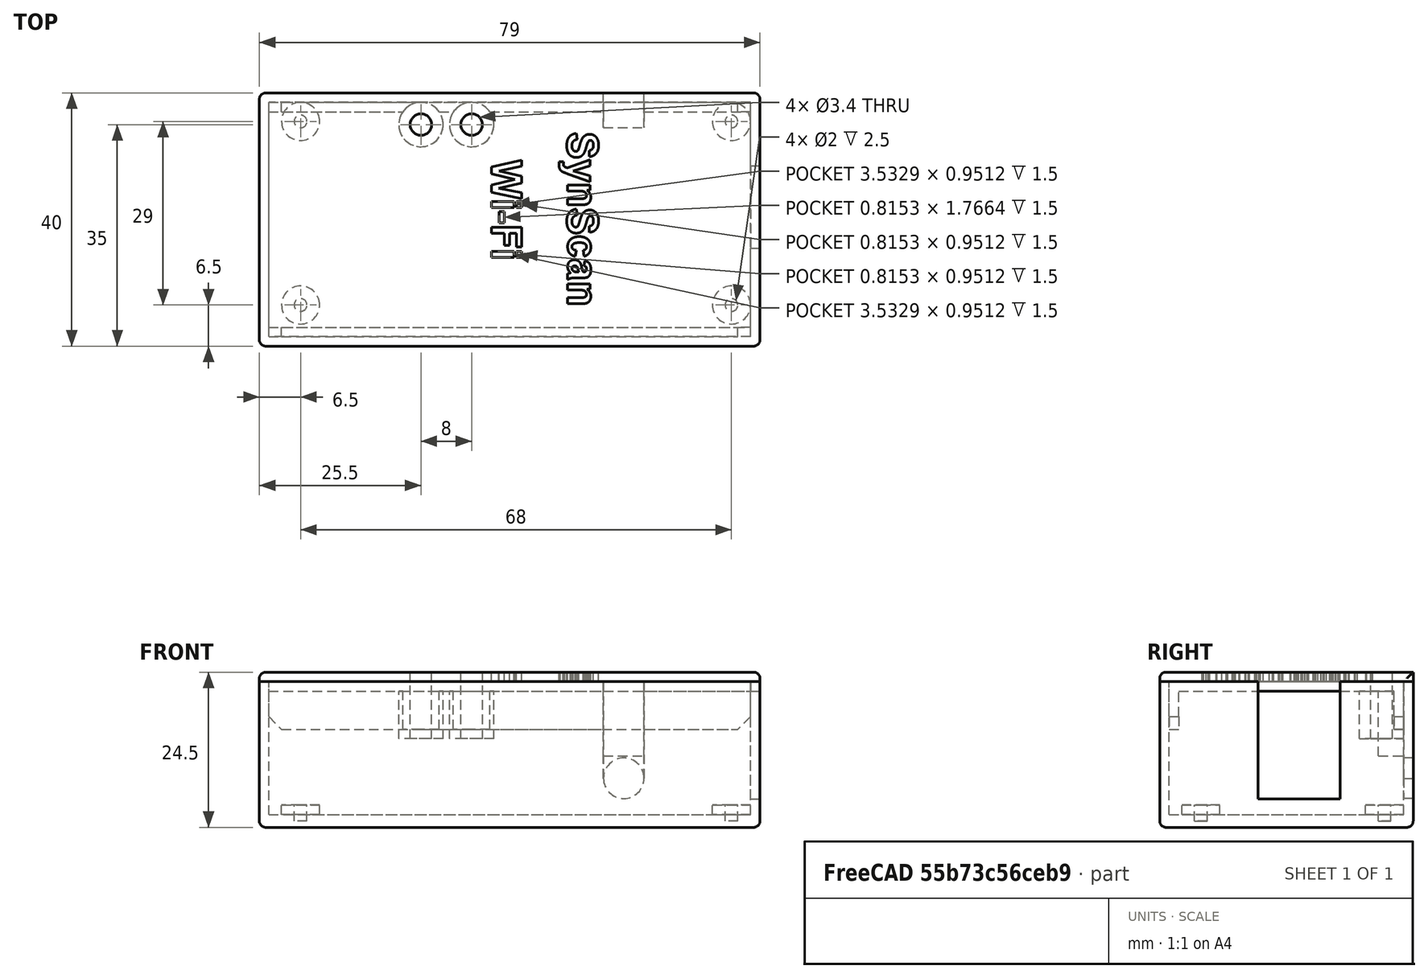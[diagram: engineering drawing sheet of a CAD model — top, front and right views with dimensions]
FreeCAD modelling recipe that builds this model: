
FCSTD DOCUMENT  (FreeCAD 0.17R13387 (Git))
Label: SynScanWiFi
License: All rights reserved
LicenseURL: http://en.wikipedia.org/wiki/All_rights_reserved
objects: Part::Cylinder×16, Part::Box×10, Part::MultiFuse×10, Part::Cut×6, Part::Part2DObjectPython×2, Part::Extrusion×2, Part::Fillet×2, Part::Chamfer×1
note: 49 computed .brp shape members not serialized (recipe doc carries the construction recipe); baked Part::Feature solids carry a one-line shape summary decoded from their .brp

FEATURE [Part::Box] Box  label="Krychle"
  AttacherType = Attacher::AttachEngine3D
  Height = 21
  Length = 76
  Placement = pos=(-39,-19.5,1.5) rot=(0,0,1;0rad)
  Width = 37
FEATURE [Part::Box] Box001  label="Krychle001"
  AttacherType = Attacher::AttachEngine3D
  Height = 23
  Length = 79
  Placement = pos=(-40.5,-21,-0.5) rot=(0,0,1;0rad)
  Width = 40
FEATURE [Part::Cut] Cut
  Base = -> Box001
  Tool = -> Box
FEATURE [Part::Cylinder] Cylinder  label="Válec"
  Angle = 360
  AttacherType = Attacher::AttachEngine3D
  Height = 3
  Placement = pos=(34,14.5,0) rot=(0,0,1;0rad)
  Radius = 1
FEATURE [Part::Cylinder] Cylinder001  label="Válec001"
  Angle = 360
  AttacherType = Attacher::AttachEngine3D
  Height = 3
  Placement = pos=(34,-14.5,0) rot=(0,0,1;0rad)
  Radius = 1
FEATURE [Part::Cylinder] Cylinder002  label="Válec002"
  Angle = 360
  AttacherType = Attacher::AttachEngine3D
  Height = 3
  Placement = pos=(-34,-14.5,0) rot=(0,0,1;0rad)
  Radius = 1
FEATURE [Part::Cylinder] Cylinder003  label="Válec003"
  Angle = 360
  AttacherType = Attacher::AttachEngine3D
  Height = 3
  Placement = pos=(-34,14.5,0) rot=(0,0,1;0rad)
  Radius = 1
FEATURE [Part::MultiFuse] Fusion  label="Diry"
  Placement = pos=(0,0,0.5) rot=(0,0,1;0rad)
  Shapes = -> [Cylinder002,Cylinder,Cylinder003,Cylinder001]
FEATURE [Part::Cylinder] Cylinder004  label="Válec004"
  Angle = 360
  AttacherType = Attacher::AttachEngine3D
  Height = 3
  Placement = pos=(34,14.5,0) rot=(0,0,1;0rad)
  Radius = 3
FEATURE [Part::Cylinder] Cylinder005  label="Válec005"
  Angle = 360
  AttacherType = Attacher::AttachEngine3D
  Height = 3
  Placement = pos=(34,-14.5,0) rot=(0,0,1;0rad)
  Radius = 3
FEATURE [Part::Cylinder] Cylinder006  label="Válec006"
  Angle = 360
  AttacherType = Attacher::AttachEngine3D
  Height = 3
  Placement = pos=(-34,14.5,0) rot=(0,0,1;0rad)
  Radius = 3
FEATURE [Part::Cylinder] Cylinder007  label="Válec007"
  Angle = 360
  AttacherType = Attacher::AttachEngine3D
  Height = 3
  Placement = pos=(-34,-14.5,0) rot=(0,0,1;0rad)
  Radius = 3
FEATURE [Part::MultiFuse] Fusion001
  Shapes = -> [Cylinder007,Cylinder004,Cylinder006,Cylinder005]
FEATURE [Part::Box] Box002  label="Krychle002"
  AttacherType = Attacher::AttachEngine3D
  Height = 19
  Length = 10
  Placement = pos=(30,-5.5,4) rot=(0,0,1;0rad)
  Width = 13
FEATURE [Part::Cylinder] Cylinder008  label="j1"
  Angle = 360
  AttacherType = Attacher::AttachEngine3D
  Height = 10
  Placement = pos=(17,21,7.25) rot=(1,0,0;1.5708rad)
  Radius = 3.2
FEATURE [Part::MultiFuse] Fusion002
  Shapes = -> [Cut,Fusion001]
FEATURE [Part::MultiFuse] Fusion003
  Shapes = -> [Fusion,Box002,Cylinder008]
FEATURE [Part::Cut] Cut001  label="Spodek "
  Base = -> Fusion002
  Tool = -> Fusion003
FEATURE [Part::Cylinder] Cylinder009  label="Válec009"
  Angle = 360
  AttacherType = Attacher::AttachEngine3D
  Height = 12
  Placement = pos=(-14,15,-10) rot=(0,0,1;0rad)
  Radius = 1.7
FEATURE [Part::Cylinder] Cylinder010  label="Válec010"
  Angle = 360
  AttacherType = Attacher::AttachEngine3D
  Height = 12
  Placement = pos=(-6,15,-10) rot=(0,0,1;0rad)
  Radius = 1.7
FEATURE [Part::Box] Box003  label="Krychle003"
  AttacherType = Attacher::AttachEngine3D
  Height = 1.5
  Length = 79
  Placement = pos=(-39.5,-20,0) rot=(0,0,1;0rad)
  Width = 40
FEATURE [Part::Box] Box004  label="Krychle004"
  AttacherType = Attacher::AttachEngine3D
  Height = 9
  Length = 76
  Placement = pos=(-38,-18.5,-7.5) rot=(0,0,1;0rad)
  Width = 37
FEATURE [Part::MultiFuse] Fusion004  label="Vicko"
  Shapes = -> [Box003,Box004]
FEATURE [Part::Part2DObjectPython] ShapeString  # Draft 2D object (typed FeaturePython)
  FontFile = <path> models/ttf/ARIALBD.TTF
  Placement = pos=(2.61625,-1.85735,24) rot=(0,0,1;0rad)
  Size = 5
  String = SynScan
  Support = -> [Fusion004]
  Tracking = 0
FEATURE [Part::Extrusion] Extrude001
  Base = -> ShapeString
  Dir = (0,0,1)
  DirMode = 2
  FaceMakerClass = Part::FaceMakerBullseye
  LengthFwd = 1.5
  LengthRev = 0
  Placement = pos=(11,16.5,-24) rot=(0,0,-1;1.5708rad)
  Solid = false
  Symmetric = false
FEATURE [Part::Part2DObjectPython] ShapeString001  # Draft 2D object (typed FeaturePython)
  FontFile = <path> models/ttf/ARIALBD.TTF
  Placement = pos=(2.62,-1.85735,24) rot=(0,0,1;0rad)
  Size = 5
  String = Wi-Fi
  Tracking = 0
FEATURE [Part::Extrusion] Extrude002
  Base = -> ShapeString001
  Dir = (0,0,1)
  DirMode = 2
  FaceMakerClass = Part::FaceMakerBullseye
  LengthFwd = 1.5
  LengthRev = 0
  Placement = pos=(-1,12,-24) rot=(0,0,-1;1.5708rad)
  Solid = false
  Symmetric = false
FEATURE [Part::Box] Box005  label="Krychle005"
  AttacherType = Attacher::AttachEngine3D
  Height = 1.5
  Length = 8.5
  Placement = pos=(31,-4.5,-1.5) rot=(0,0,1;0rad)
  Width = 13
FEATURE [Part::Box] Box006  label="Krychle006"
  AttacherType = Attacher::AttachEngine3D
  Height = 6
  Length = 76
  Placement = pos=(-38,-17,-7.5) rot=(0,0,1;0rad)
  Width = 34
FEATURE [Part::MultiFuse] Fusion005
  Shapes = -> [Box006,Cylinder009,Cylinder010,Extrude001,Extrude002]
FEATURE [Part::Cut] Cut002
  Base = -> Fusion004
  Tool = -> Fusion005
FEATURE [Part::Cylinder] Cylinder011  label="Válec011"
  Angle = 360
  AttacherType = Attacher::AttachEngine3D
  Height = 12
  Placement = pos=(-6,15,-10) rot=(0,0,1;0rad)
  Radius = 1.7
FEATURE [Part::Cylinder] Cylinder012  label="Válec012"
  Angle = 360
  AttacherType = Attacher::AttachEngine3D
  Height = 12
  Placement = pos=(-14,15,-10) rot=(0,0,1;0rad)
  Radius = 1.7
FEATURE [Part::Cylinder] Cylinder013  label="Válec013"
  Angle = 360
  AttacherType = Attacher::AttachEngine3D
  Height = 10
  Placement = pos=(-6,15,-9) rot=(0,0,1;0rad)
  Radius = 3.5
FEATURE [Part::Cylinder] Cylinder014  label="Válec014"
  Angle = 360
  AttacherType = Attacher::AttachEngine3D
  Height = 10
  Placement = pos=(-14,15,-9) rot=(0,0,1;0rad)
  Radius = 3.5
FEATURE [Part::MultiFuse] Fusion007
  Shapes = -> [Cylinder011,Cylinder012]
FEATURE [Part::Box] Box018  label="jK1"
  AttacherType = Attacher::AttachEngine3D
  Height = 15.25
  Length = 6.4
  Placement = pos=(13.8,11,7.25) rot=(0,0,1;0rad)
  Width = 10
FEATURE [Part::Cylinder] Cylinder015  label="j002"
  Angle = 360
  AttacherType = Attacher::AttachEngine3D
  Height = 10
  Placement = pos=(17,21,7.25) rot=(1,0,0;1.5708rad)
  Radius = 3.2
FEATURE [Part::Box] Box019  label="jK002"
  AttacherType = Attacher::AttachEngine3D
  Height = 15.25
  Length = 6.4
  Placement = pos=(13.8,17.5,7.25) rot=(0,0,1;0rad)
  Width = 1.5
FEATURE [Part::Cut] Cut004
  Base = -> Cut001
  Tool = -> Box018
FEATURE [Part::MultiFuse] Fusion008
  Shapes = -> [Cylinder013,Cylinder014,Box005,Cut002]
FEATURE [Part::Cut] Cut005
  Base = -> Fusion008
  Placement = pos=(-1,-1,22.5) rot=(0,0,1;0rad)
  Tool = -> Fusion007
FEATURE [Part::Box] Box020  label="jK003"
  AttacherType = Attacher::AttachEngine3D
  Height = 10.75
  Length = 6.4
  Placement = pos=(13.8,13.5,10.75) rot=(0,0,1;0rad)
  Width = 5.5
FEATURE [Part::MultiFuse] Fusion009
  Shapes = -> [Box019,Box020]
FEATURE [Part::Cut] Cut006
  Base = -> Fusion009
  Tool = -> Cylinder015
FEATURE [Part::MultiFuse] Fusion010
  Shapes = -> [Cut006,Cut005]
FEATURE [Part::Fillet] Fillet  label="SynScanBWiFi"
  Base = -> Cut004
  Edges = 8 edges r=1: [Edge1,Edge3,Edge4,Edge5,Edge6,Edge16,Edge21,Edge22]
FEATURE [Part::Fillet] Fillet001
  Base = -> Fusion010
  Edges = 7 edges r=1: [Edge80,Edge83,Edge98,Edge99,Edge102,Edge103,Edge104]
FEATURE [Part::Chamfer] Chamfer  label="SynScanTWiFi"
  Base = -> Fillet001
  Edges = 4 edges r=2: [Edge42,Edge46,Edge58,Edge323]
note: 2 file-system paths scrubbed to <path> (originals preserved in the JSON sidecar)
